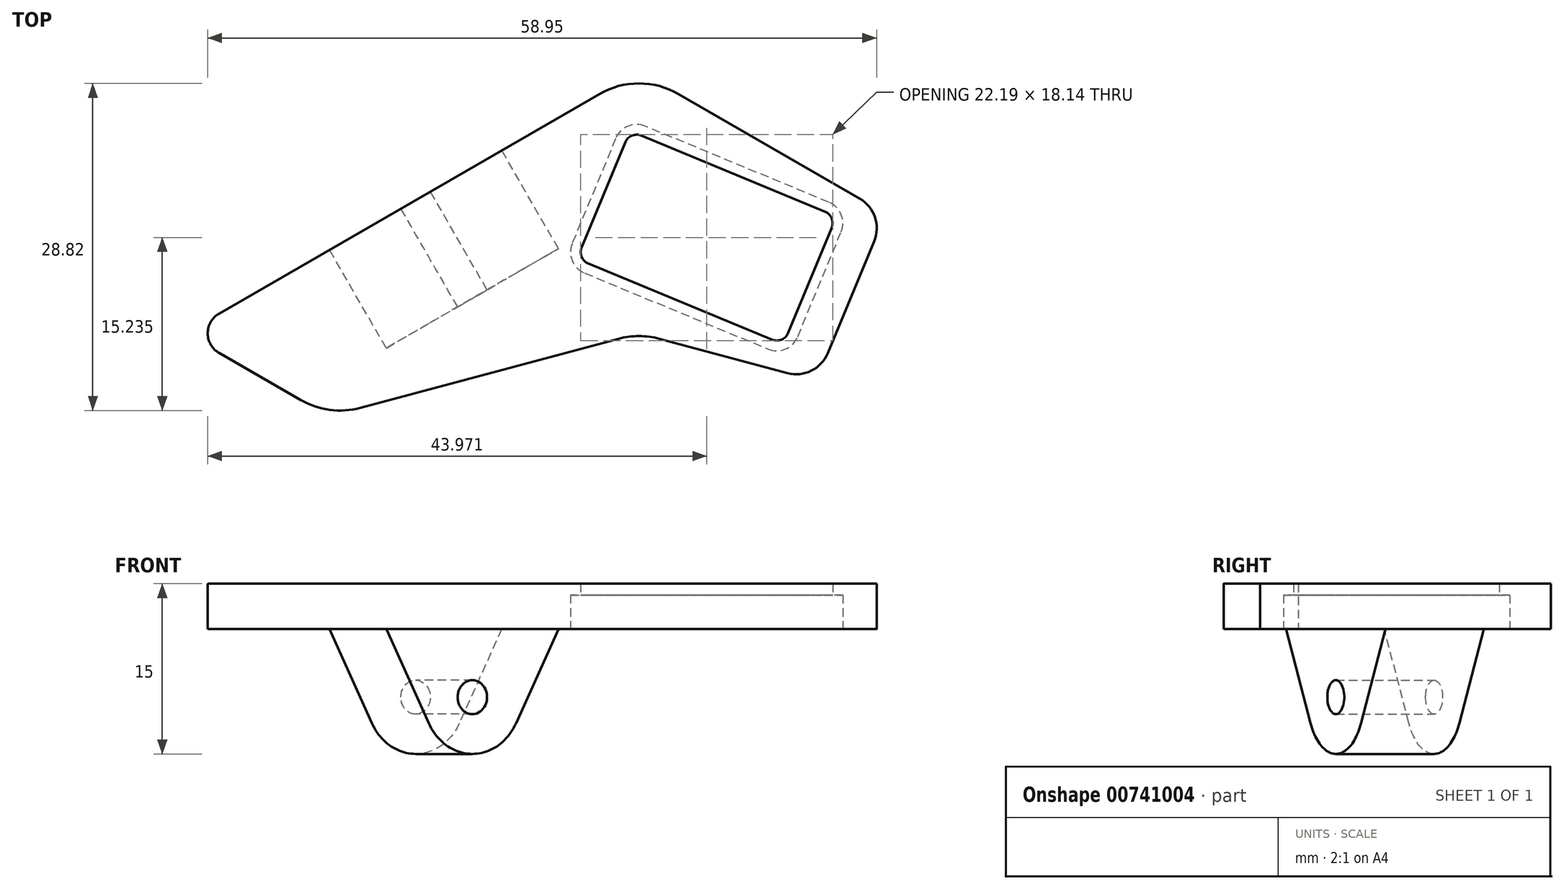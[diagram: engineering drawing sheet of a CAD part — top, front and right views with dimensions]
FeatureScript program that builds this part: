
annotation { "Feature Type Name" : "Feature", "Feature Type Description" : "" }
export const myFeature = defineFeature(function(context is Context, id is Id, definition is map)
    precondition{}
    {
        {
            var Q0;
            Q0=qCreatedBy(makeId("Top.planeOp"),FACE);
            var sketch = newSketch(context, id + "F0", { "sketchPlane" : qUnion([Q0])});
            skLineSegment(sketch, "E0", {"start": v(-37, 1.73) * mm, "end": v(-3.5, 21.07) * mm});
            skLineSegment(sketch, "E1", {"start": v(40, 0) * mm, "end": v(21.73, 10.55) * mm, "construction": true});
            skLineSegment(sketch, "E2", {"start": v(-1.81, -0.49) * mm, "end": v(-24.52, -6.57) * mm});
            skLineSegment(sketch, "E3", {"start": v(0, 0) * mm, "end": v(0, 23.1) * mm, "construction": true});
            skLineSegment(sketch, "E4", {"start": v(40, 0) * mm, "end": v(27.32, -7.32) * mm, "construction": true});
            skLineSegment(sketch, "E5", {"start": v(-29.83, -5.87) * mm, "end": v(-40, 0) * mm});
            skLineSegment(sketch, "E6", {"start": v(27.32, -7.32) * mm, "end": v(0, -23.1) * mm, "construction": true});
            skLineSegment(sketch, "E7", {"start": v(0, -23.1) * mm, "end": v(-37, -1.73) * mm, "construction": true});
            skLineSegment(sketch, "E8", {"start": v(13.99, -0.3) * mm, "end": v(17.82, 8.93) * mm});
            skLineSegment(sketch, "E9", {"start": v(16.73, 11.54) * mm, "end": v(0.57, 18.24) * mm});
            skLineSegment(sketch, "E10", {"start": v(-2.05, 17.16) * mm, "end": v(-5.87, 7.92) * mm});
            skLineSegment(sketch, "E11", {"start": v(-4.8, 5.3) * mm, "end": v(11.38, -1.4) * mm});
            skPoint(sketch, "E12.visualSharp", {"position": v(-6.64, 6.07) * mm});
            skArc(sketch, "E12.filletArc", {"start": v(-5.87, 7.92) * mm, "mid": v(-5.87, 6.39) * mm, "end": v(-4.8, 5.3) * mm});
            skPoint(sketch, "E13.visualSharp", {"position": v(-1.28, 19) * mm});
            skArc(sketch, "E13.filletArc", {"start": v(0.57, 18.24) * mm, "mid": v(-0.96, 18.24) * mm, "end": v(-2.05, 17.16) * mm});
            skPoint(sketch, "E14.visualSharp", {"position": v(18.58, 10.78) * mm});
            skArc(sketch, "E14.filletArc", {"start": v(17.82, 8.93) * mm, "mid": v(17.82, 10.46) * mm, "end": v(16.73, 11.54) * mm});
            skPoint(sketch, "E15.visualSharp", {"position": v(13.22, -2.16) * mm});
            skArc(sketch, "E15.filletArc", {"start": v(11.38, -1.4) * mm, "mid": v(12.9, -1.4) * mm, "end": v(13.99, -0.3) * mm});
            skLineSegment(sketch, "E16", {"start": v(16.64, -1.76) * mm, "end": v(20.73, 8.12) * mm});
            skLineSegment(sketch, "E17", {"start": v(15.63, -4.19) * mm, "end": v(27.32, -7.32) * mm, "construction": true});
            skLineSegment(sketch, "E18", {"start": v(13.09, -3.5) * mm, "end": v(1.81, -0.49) * mm});
            skLineSegment(sketch, "E19", {"start": v(3.5, 21.07) * mm, "end": v(19.45, 11.86) * mm});
            skPoint(sketch, "E20.visualSharp", {"position": v(15.63, -4.19) * mm});
            skArc(sketch, "E20.filletArc", {"start": v(13.09, -3.5) * mm, "mid": v(15.2, -3.3) * mm, "end": v(16.64, -1.76) * mm});
            skPoint(sketch, "E21.visualSharp", {"position": v(21.73, 10.55) * mm});
            skArc(sketch, "E21.filletArc", {"start": v(20.73, 8.12) * mm, "mid": v(20.8, 10.23) * mm, "end": v(19.45, 11.86) * mm});
            skPoint(sketch, "E22.visualSharp", {"position": v(0, 0) * mm});
            skArc(sketch, "E22.filletArc", {"start": v(1.81, -0.49) * mm, "mid": v(0, -0.25) * mm, "end": v(-1.81, -0.49) * mm});
            skPoint(sketch, "E23.visualSharp", {"position": v(-27.32, -7.32) * mm});
            skArc(sketch, "E23.filletArc", {"start": v(-29.83, -5.87) * mm, "mid": v(-27.25, -6.75) * mm, "end": v(-24.52, -6.57) * mm});
            skPoint(sketch, "E24.visualSharp", {"position": v(0, 23.1) * mm});
            skArc(sketch, "E24.filletArc", {"start": v(3.5, 21.07) * mm, "mid": v(0, 22.01) * mm, "end": v(-3.5, 21.07) * mm});
            skPoint(sketch, "E25.visualSharp", {"position": v(-40, 0) * mm});
            skArc(sketch, "E25.filletArc", {"start": v(-37, 1.73) * mm, "mid": v(-38, 0) * mm, "end": v(-37, -1.73) * mm});
            skSolve(sketch);
        }
        {
            var Q0;
            Q0=makeQuery(id+"F0.imprint","IMPRINT",FACE,{"disambiguationData":[TD([[makeQuery(id+"F0.imprint","IMPRINT",EDGE,{"derivedFrom":sQuery(id+"F0.wireOp",EDGE,"E0")}),-1.0]])]});
            extrude(context, id + "F1", {"entities" : qUnion([Q0]), "depth" : 3 * mm, "offsetDistance" : 25 * mm});
        }
        {
            var Q0;
            Q0=makeQuery(id+"F1.opExtrude","CAP_FACE",FACE,{"disambiguationData":[OSD([sQuery(id+"F0.wireOp",EDGE,"E0"),sQuery(id+"F0.wireOp",EDGE,"E2"),sQuery(id+"F0.wireOp",EDGE,"E5"),sQuery(id+"F0.wireOp",EDGE,"E8"),sQuery(id+"F0.wireOp",EDGE,"E9"),sQuery(id+"F0.wireOp",EDGE,"E10"),sQuery(id+"F0.wireOp",EDGE,"E11"),sQuery(id+"F0.wireOp",EDGE,"E12.filletArc"),sQuery(id+"F0.wireOp",EDGE,"E13.filletArc"),sQuery(id+"F0.wireOp",EDGE,"E14.filletArc"),sQuery(id+"F0.wireOp",EDGE,"E15.filletArc"),sQuery(id+"F0.wireOp",EDGE,"E16"),sQuery(id+"F0.wireOp",EDGE,"E18"),sQuery(id+"F0.wireOp",EDGE,"E19"),sQuery(id+"F0.wireOp",EDGE,"E20.filletArc"),sQuery(id+"F0.wireOp",EDGE,"E21.filletArc"),sQuery(id+"F0.wireOp",EDGE,"E22.filletArc"),sQuery(id+"F0.wireOp",EDGE,"E23.filletArc"),sQuery(id+"F0.wireOp",EDGE,"E24.filletArc"),sQuery(id+"F0.wireOp",EDGE,"E25.filletArc")])],"isStart":false});
            var sketch = newSketch(context, id + "F2", { "sketchPlane" : qUnion([Q0])});
            skArc(sketch, "E26.0", {"start": v(-5.04, 7.58) * mm, "mid": v(-5.04, 6.73) * mm, "end": v(-4.45, 6.14) * mm});
            skLineSegment(sketch, "E26.1", {"start": v(-1.22, 16.81) * mm, "end": v(-5.04, 7.58) * mm});
            skLineSegment(sketch, "E26.2", {"start": v(-4.45, 6.14) * mm, "end": v(11.72, -0.56) * mm});
            skArc(sketch, "E26.3", {"start": v(0.22, 17.4) * mm, "mid": v(-0.62, 17.4) * mm, "end": v(-1.22, 16.81) * mm});
            skArc(sketch, "E26.4", {"start": v(11.72, -0.56) * mm, "mid": v(12.56, -0.56) * mm, "end": v(13.16, 0.04) * mm});
            skLineSegment(sketch, "E26.5", {"start": v(13.16, 0.04) * mm, "end": v(16.98, 9.28) * mm});
            skArc(sketch, "E26.6", {"start": v(16.98, 9.28) * mm, "mid": v(16.98, 10.12) * mm, "end": v(16.39, 10.71) * mm});
            skLineSegment(sketch, "E26.7", {"start": v(16.39, 10.71) * mm, "end": v(0.22, 17.4) * mm});
            skLineSegment(sketch, "E27.0", {"start": v(13.09, -3.5) * mm, "end": v(1.81, -0.49) * mm});
            skArc(sketch, "E28.0", {"start": v(13.09, -3.5) * mm, "mid": v(15.2, -3.3) * mm, "end": v(16.64, -1.76) * mm});
            skLineSegment(sketch, "E29.0", {"start": v(16.64, -1.76) * mm, "end": v(20.73, 8.12) * mm});
            skArc(sketch, "E30.0", {"start": v(20.73, 8.12) * mm, "mid": v(20.8, 10.23) * mm, "end": v(19.45, 11.86) * mm});
            skLineSegment(sketch, "E31.0", {"start": v(3.5, 21.07) * mm, "end": v(19.45, 11.86) * mm});
            skArc(sketch, "E32.0", {"start": v(3.5, 21.07) * mm, "mid": v(0, 22.01) * mm, "end": v(-3.5, 21.07) * mm});
            skLineSegment(sketch, "E33.0", {"start": v(-37, 1.73) * mm, "end": v(-3.5, 21.07) * mm});
            skArc(sketch, "E34.0", {"start": v(-37, 1.73) * mm, "mid": v(-38, 0) * mm, "end": v(-37, -1.73) * mm});
            skLineSegment(sketch, "E35.0", {"start": v(-29.83, -5.87) * mm, "end": v(-37, -1.73) * mm});
            skArc(sketch, "E36.0", {"start": v(-29.83, -5.87) * mm, "mid": v(-27.25, -6.75) * mm, "end": v(-24.52, -6.57) * mm});
            skLineSegment(sketch, "E37.0", {"start": v(-1.81, -0.49) * mm, "end": v(-24.52, -6.57) * mm});
            skArc(sketch, "E38.0", {"start": v(1.81, -0.49) * mm, "mid": v(0, -0.25) * mm, "end": v(-1.81, -0.49) * mm});
            skSolve(sketch);
        }
        {
            var Q0;
            Q0 = qSketchRegion(id + "F2", true);
            extrude(context, id + "F3", {"entities" : qUnion([Q0]), "operationType" : NewBodyOperationType.ADD, "depth" : 1 * mm, "offsetDistance" : 25 * mm});
        }
        {
            var Q0;
            Q0=makeQuery(id+"F1.opExtrude","CAP_FACE",FACE,{"disambiguationData":[OSD([sQuery(id+"F0.wireOp",EDGE,"E0"),sQuery(id+"F0.wireOp",EDGE,"E2"),sQuery(id+"F0.wireOp",EDGE,"E5"),sQuery(id+"F0.wireOp",EDGE,"E8"),sQuery(id+"F0.wireOp",EDGE,"E9"),sQuery(id+"F0.wireOp",EDGE,"E10"),sQuery(id+"F0.wireOp",EDGE,"E11"),sQuery(id+"F0.wireOp",EDGE,"E12.filletArc"),sQuery(id+"F0.wireOp",EDGE,"E13.filletArc"),sQuery(id+"F0.wireOp",EDGE,"E14.filletArc"),sQuery(id+"F0.wireOp",EDGE,"E15.filletArc"),sQuery(id+"F0.wireOp",EDGE,"E16"),sQuery(id+"F0.wireOp",EDGE,"E18"),sQuery(id+"F0.wireOp",EDGE,"E19"),sQuery(id+"F0.wireOp",EDGE,"E20.filletArc"),sQuery(id+"F0.wireOp",EDGE,"E21.filletArc"),sQuery(id+"F0.wireOp",EDGE,"E22.filletArc"),sQuery(id+"F0.wireOp",EDGE,"E23.filletArc"),sQuery(id+"F0.wireOp",EDGE,"E24.filletArc"),sQuery(id+"F0.wireOp",EDGE,"E25.filletArc")])],"isStart":true});
            var sketch = newSketch(context, id + "F4", { "sketchPlane" : qUnion([Q0])});
            skLineSegment(sketch, "E39.0", {"start": v(-29.83, 5.87) * mm, "end": v(-37, 1.73) * mm});
            skArc(sketch, "E40.0", {"start": v(-29.83, 5.87) * mm, "mid": v(-27.25, 6.75) * mm, "end": v(-24.52, 6.57) * mm});
            skArc(sketch, "E41.0", {"start": v(-37, -1.73) * mm, "mid": v(-38, 0) * mm, "end": v(-37, 1.73) * mm});
            skLineSegment(sketch, "E42.0", {"start": v(-1.81, 0.49) * mm, "end": v(-24.52, 6.57) * mm});
            skLineSegment(sketch, "E43.0", {"start": v(-37, -1.73) * mm, "end": v(-24.97, -8.68) * mm});
            skLineSegment(sketch, "E44", {"start": v(-24.97, -8.68) * mm, "end": v(-17.31, -2.25) * mm});
            skLineSegment(sketch, "E45", {"start": v(-17.31, -2.25) * mm, "end": v(-1.81, 0.49) * mm});
            skPoint(sketch, "E46.orphan", {"position": v(-3.5, -21.07) * mm});
            skSolve(sketch);
        }
        {
            var Q0;
            Q0=makeQuery(id+"F1.opExtrude","SWEPT_FACE",FACE,{"disambiguationData":[OSD([sQuery(id+"F0.wireOp",EDGE,"E0")])]});
            var sketch = newSketch(context, id + "F5", { "sketchPlane" : qUnion([Q0])});
            skCircle(sketch, "E47", {"center": v(11.18, -6) * mm, "radius": 1.5 * mm});
            skCircle(sketch, "E48", {"center": v(11.18, -6) * mm, "radius": 5 * mm});
            skLineSegment(sketch, "E49", {"start": v(15.61, -8.3) * mm, "end": v(19.94, 0) * mm});
            skLineSegment(sketch, "E50", {"start": v(19.94, 0) * mm, "end": v(2.42, 0) * mm});
            skLineSegment(sketch, "E51", {"start": v(2.42, 0) * mm, "end": v(6.74, -8.3) * mm});
            skSolve(sketch);
        }
        {
            var Q0;
            Q0 = qSketchRegion(id + "F5", true);
            extrude(context, id + "F6", {"entities" : qUnion([Q0]), "operationType" : NewBodyOperationType.ADD, "oppositeDirection" : true, "depth" : 10 * mm, "offsetDistance" : 25 * mm});
        }
    });
